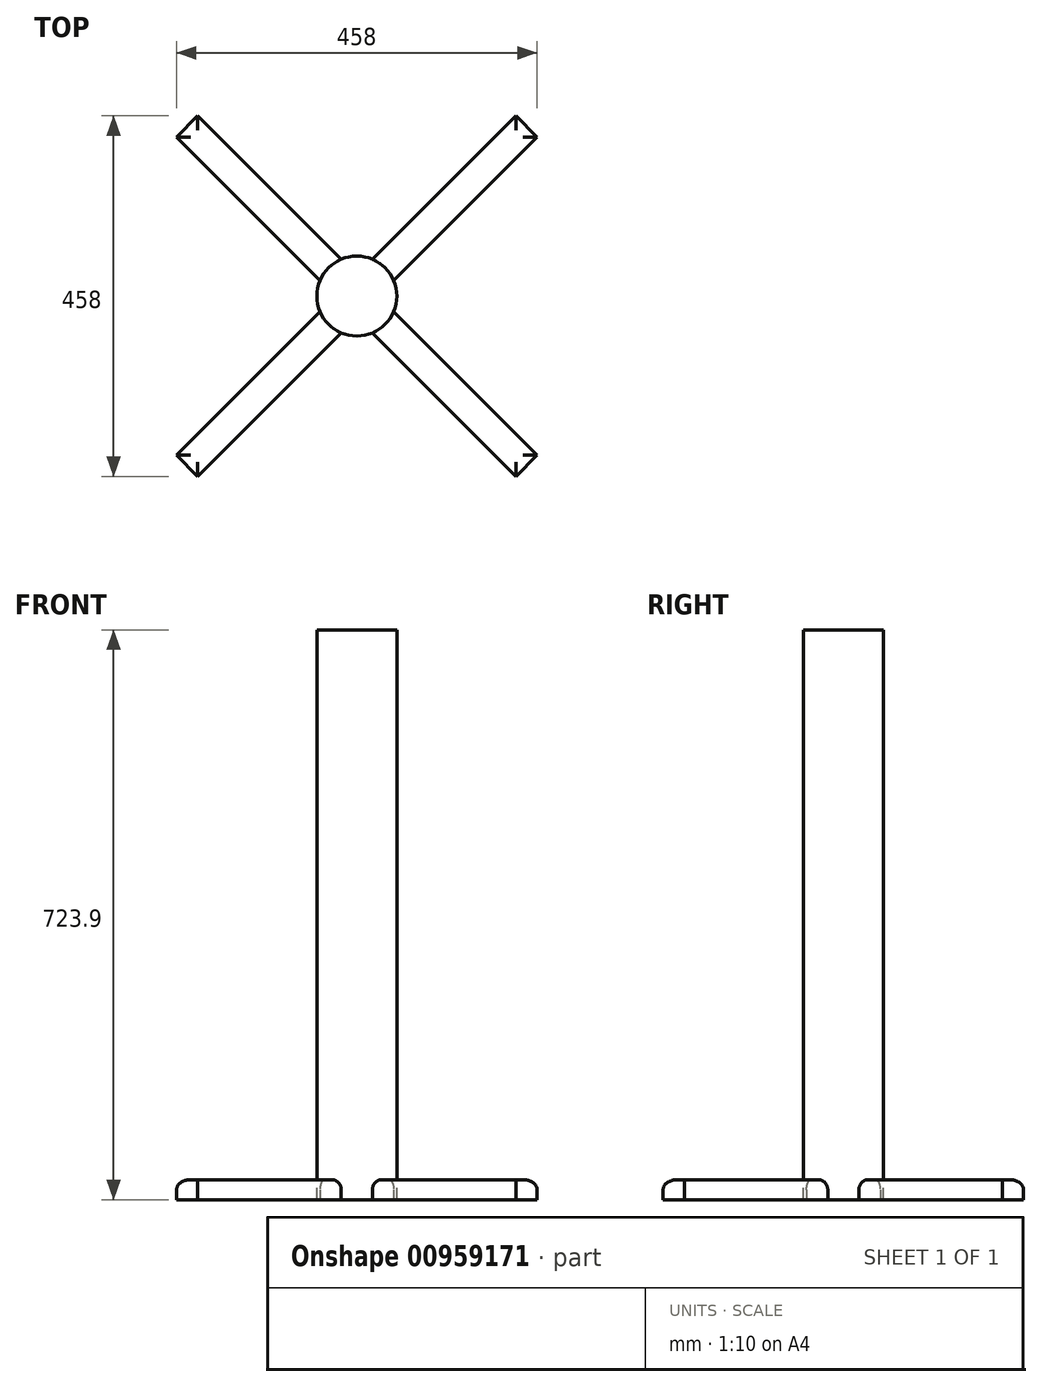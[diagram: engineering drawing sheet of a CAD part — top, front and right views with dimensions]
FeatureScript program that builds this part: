
annotation { "Feature Type Name" : "Feature", "Feature Type Description" : "" }
export const myFeature = defineFeature(function(context is Context, id is Id, definition is map)
    precondition{}
    {
        {
            var Q0;
            Q0=qCreatedBy(makeId("Top.planeOp"),FACE);
            var sketch = newSketch(context, id + "F0", { "sketchPlane" : qUnion([Q0])});
            skCircle(sketch, "E0", {"center": v(0, 0) * mm, "radius": 50.8 * mm});
            skSolve(sketch);
        }
        {
            var Q0;
            Q0 = qSketchRegion(id + "F0", true);
            extrude(context, id + "F1", {"entities" : qUnion([Q0]), "oppositeDirection" : true, "depth" : 723.9 * mm, "offsetDistance" : 25.4 * mm});
        }
        {
            var Q0;
            Q0=makeQuery(id+"F1.opExtrude","CAP_FACE",FACE,{"disambiguationData":[OSD([sQuery(id+"F0.wireOp",EDGE,"E0")])],"isStart":false});
            var sketch = newSketch(context, id + "F2", { "sketchPlane" : qUnion([Q0])});
            skLineSegment(sketch, "E1", {"start": v(0, 0) * mm, "end": v(0, 239.02) * mm, "construction": true});
            skLineSegment(sketch, "E2.0", {"start": v(-13.47, -13.47) * mm, "end": v(-229, 202.06) * mm});
            skLineSegment(sketch, "E3.0", {"start": v(13.47, 13.47) * mm, "end": v(-202.06, 229) * mm});
            skLineSegment(sketch, "E4", {"start": v(-229, 202.06) * mm, "end": v(-202.06, 229) * mm});
            skLineSegment(sketch, "E5", {"start": v(13.47, 13.47) * mm, "end": v(-13.47, -13.47) * mm});
            skLineSegment(sketch, "E6.1.0", {"start": v(-13.47, 13.47) * mm, "end": v(-229, -202.06) * mm});
            skLineSegment(sketch, "E6.1.1", {"start": v(-202.06, -229) * mm, "end": v(-229, -202.06) * mm});
            skLineSegment(sketch, "E6.1.2", {"start": v(13.47, -13.47) * mm, "end": v(-202.06, -229) * mm});
            skLineSegment(sketch, "E6.1.3", {"start": v(-13.47, 13.47) * mm, "end": v(13.47, -13.47) * mm});
            skLineSegment(sketch, "E6.2.0", {"start": v(-13.47, -13.47) * mm, "end": v(202.06, -229) * mm});
            skLineSegment(sketch, "E6.2.1", {"start": v(229, -202.06) * mm, "end": v(202.06, -229) * mm});
            skLineSegment(sketch, "E6.2.2", {"start": v(13.47, 13.47) * mm, "end": v(229, -202.06) * mm});
            skLineSegment(sketch, "E6.2.3", {"start": v(-13.47, -13.47) * mm, "end": v(13.47, 13.47) * mm});
            skLineSegment(sketch, "E6.3.0", {"start": v(13.47, -13.47) * mm, "end": v(229, 202.06) * mm});
            skLineSegment(sketch, "E6.3.1", {"start": v(202.06, 229) * mm, "end": v(229, 202.06) * mm});
            skLineSegment(sketch, "E6.3.2", {"start": v(-13.47, 13.47) * mm, "end": v(202.06, 229) * mm});
            skLineSegment(sketch, "E6.3.3", {"start": v(13.47, -13.47) * mm, "end": v(-13.47, 13.47) * mm});
            skPoint(sketch, "E6.center", {"position": v(0, 0) * mm});
            skSolve(sketch);
        }
        {
            var Q0;
            {var subQ0=sQuery(id+"F2.wireOp",EDGE,"E4");Q0=makeQuery(id+"F2.imprint","IMPRINT",FACE,{"disambiguationData":[TD([[makeQuery(id+"F2.imprint","IMPRINT",EDGE,{"derivedFrom":subQ0}),-1.0]])]});}
            var Q1;
            {var subQ0=sQuery(id+"F2.wireOp",EDGE,"E6.3.1");Q1=makeQuery(id+"F2.imprint","IMPRINT",FACE,{"disambiguationData":[TD([[makeQuery(id+"F2.imprint","IMPRINT",EDGE,{"derivedFrom":subQ0}),-1.0]])]});}
            var Q2;
            {var subQ0=sQuery(id+"F2.wireOp",EDGE,"E6.2.1");Q2=makeQuery(id+"F2.imprint","IMPRINT",FACE,{"disambiguationData":[TD([[makeQuery(id+"F2.imprint","IMPRINT",EDGE,{"derivedFrom":subQ0}),-1.0]])]});}
            var Q3;
            {var subQ0=sQuery(id+"F2.wireOp",EDGE,"E6.1.1");Q3=makeQuery(id+"F2.imprint","IMPRINT",FACE,{"disambiguationData":[TD([[makeQuery(id+"F2.imprint","IMPRINT",EDGE,{"derivedFrom":subQ0}),-1.0]])]});}
            extrude(context, id + "F3", {"entities" : qUnion([Q0, Q1, Q2, Q3]), "operationType" : NewBodyOperationType.ADD, "oppositeDirection" : true, "depth" : 25.4 * mm, "offsetDistance" : 25.4 * mm});
        }
        {
            var Q0;
            Q0=makeQuery(id+"F3.opExtrude","CAP_EDGE",EDGE,{"disambiguationData":[OSD([sQuery(id+"F2.wireOp",EDGE,"E3.0")])],"isStart":false});
            var Q1;
            Q1=makeQuery(id+"F3.opExtrude","CAP_EDGE",EDGE,{"disambiguationData":[OSD([sQuery(id+"F2.wireOp",EDGE,"E4")])],"isStart":false});
            var Q2;
            Q2=makeQuery(id+"F3.opExtrude","CAP_EDGE",EDGE,{"disambiguationData":[OSD([sQuery(id+"F2.wireOp",EDGE,"E2.0")])],"isStart":false});
            var Q3;
            Q3=makeQuery(id+"F3.opExtrude","CAP_EDGE",EDGE,{"disambiguationData":[OSD([sQuery(id+"F2.wireOp",EDGE,"E6.1.0")])],"isStart":false});
            var Q4;
            Q4=makeQuery(id+"F3.opExtrude","CAP_EDGE",EDGE,{"disambiguationData":[OSD([sQuery(id+"F2.wireOp",EDGE,"E6.1.1")])],"isStart":false});
            var Q5;
            Q5=makeQuery(id+"F3.opExtrude","CAP_EDGE",EDGE,{"disambiguationData":[OSD([sQuery(id+"F2.wireOp",EDGE,"E6.1.2")])],"isStart":false});
            var Q6;
            Q6=makeQuery(id+"F3.opExtrude","CAP_EDGE",EDGE,{"disambiguationData":[OSD([sQuery(id+"F2.wireOp",EDGE,"E6.2.0")])],"isStart":false});
            var Q7;
            Q7=makeQuery(id+"F3.opExtrude","CAP_EDGE",EDGE,{"disambiguationData":[OSD([sQuery(id+"F2.wireOp",EDGE,"E6.2.2")])],"isStart":false});
            var Q8;
            Q8=makeQuery(id+"F3.opExtrude","CAP_EDGE",EDGE,{"disambiguationData":[OSD([sQuery(id+"F2.wireOp",EDGE,"E6.2.1")])],"isStart":false});
            var Q9;
            Q9=makeQuery(id+"F3.opExtrude","CAP_EDGE",EDGE,{"disambiguationData":[OSD([sQuery(id+"F2.wireOp",EDGE,"E6.3.0")])],"isStart":false});
            var Q10;
            Q10=makeQuery(id+"F3.opExtrude","CAP_EDGE",EDGE,{"disambiguationData":[OSD([sQuery(id+"F2.wireOp",EDGE,"E6.3.2")])],"isStart":false});
            var Q11;
            Q11=makeQuery(id+"F3.opExtrude","CAP_EDGE",EDGE,{"disambiguationData":[OSD([sQuery(id+"F2.wireOp",EDGE,"E6.3.1")])],"isStart":false});
            fillet(context, id + "F4", {"entities" : qUnion([Q0, Q1, Q2, Q3, Q4, Q5, Q6, Q7, Q8, Q9, Q10, Q11]), "radius" : 12.7 * mm, "tangentPropagation" : true, "allowEdgeOverflow" : false});
        }
        {
            var Q0;
            Q0=makeQuery(id+"F1.opExtrude","SWEPT_BODY",BODY,{"disambiguationData":[OSD([sQuery(id+"F0.wireOp",EDGE,"E0")])]});
            transform(context, id + "F5", {"entities" : qUnion([Q0]), "transformType" : TransformType.TRANSLATION_3D, "dx" : 0 * mm, "dy" : 0 * mm, "dz" : 0 * mm, "makeCopy" : true});
        }
        {
            var Q0;
            Q0=makeQuery(id+"F5.opPattern","COPY",BODY,{"derivedFrom":makeQuery(id+"F1.opExtrude","SWEPT_BODY",BODY,{"disambiguationData":[OSD([sQuery(id+"F0.wireOp",EDGE,"E0")])]}),"instanceName":"1"});
            deleteBodies(context, id + "F6", {"entities" : qUnion([Q0])});
        }
    });
